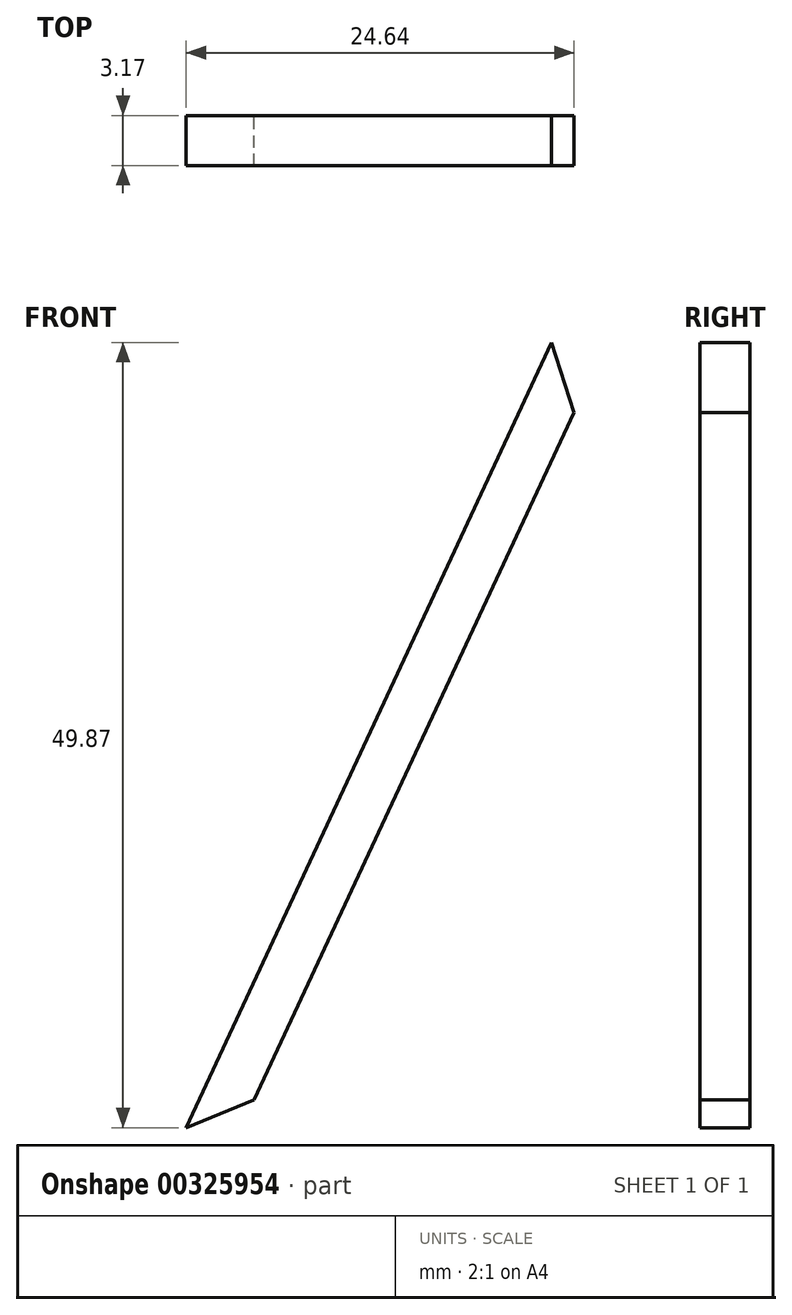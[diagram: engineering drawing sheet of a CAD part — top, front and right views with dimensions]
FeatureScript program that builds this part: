
annotation { "Feature Type Name" : "Feature", "Feature Type Description" : "" }
export const myFeature = defineFeature(function(context is Context, id is Id, definition is map)
    precondition{}
    {
        {
            var Q0;
            Q0=qCreatedBy(makeId("Front.planeOp"),FACE);
            var sketch = newSketch(context, id + "F0", { "sketchPlane" : qUnion([Q0])});
            skLineSegment(sketch, "E0", {"start": v(0, 0) * mm, "end": v(23.2, 49.87) * mm});
            skLineSegment(sketch, "E1", {"start": v(23.2, 49.87) * mm, "end": v(24.64, 45.44) * mm});
            skLineSegment(sketch, "E2", {"start": v(0, 0) * mm, "end": v(4.32, 1.75) * mm});
            skLineSegment(sketch, "E3", {"start": v(4.32, 1.75) * mm, "end": v(24.64, 45.44) * mm});
            skSolve(sketch);
        }
        {
            var Q0;
            Q0 = qSketchRegion(id + "F0", true);
            extrude(context, id + "F1", {"entities" : qUnion([Q0]), "depth" : 3.17 * mm});
        }
    });
